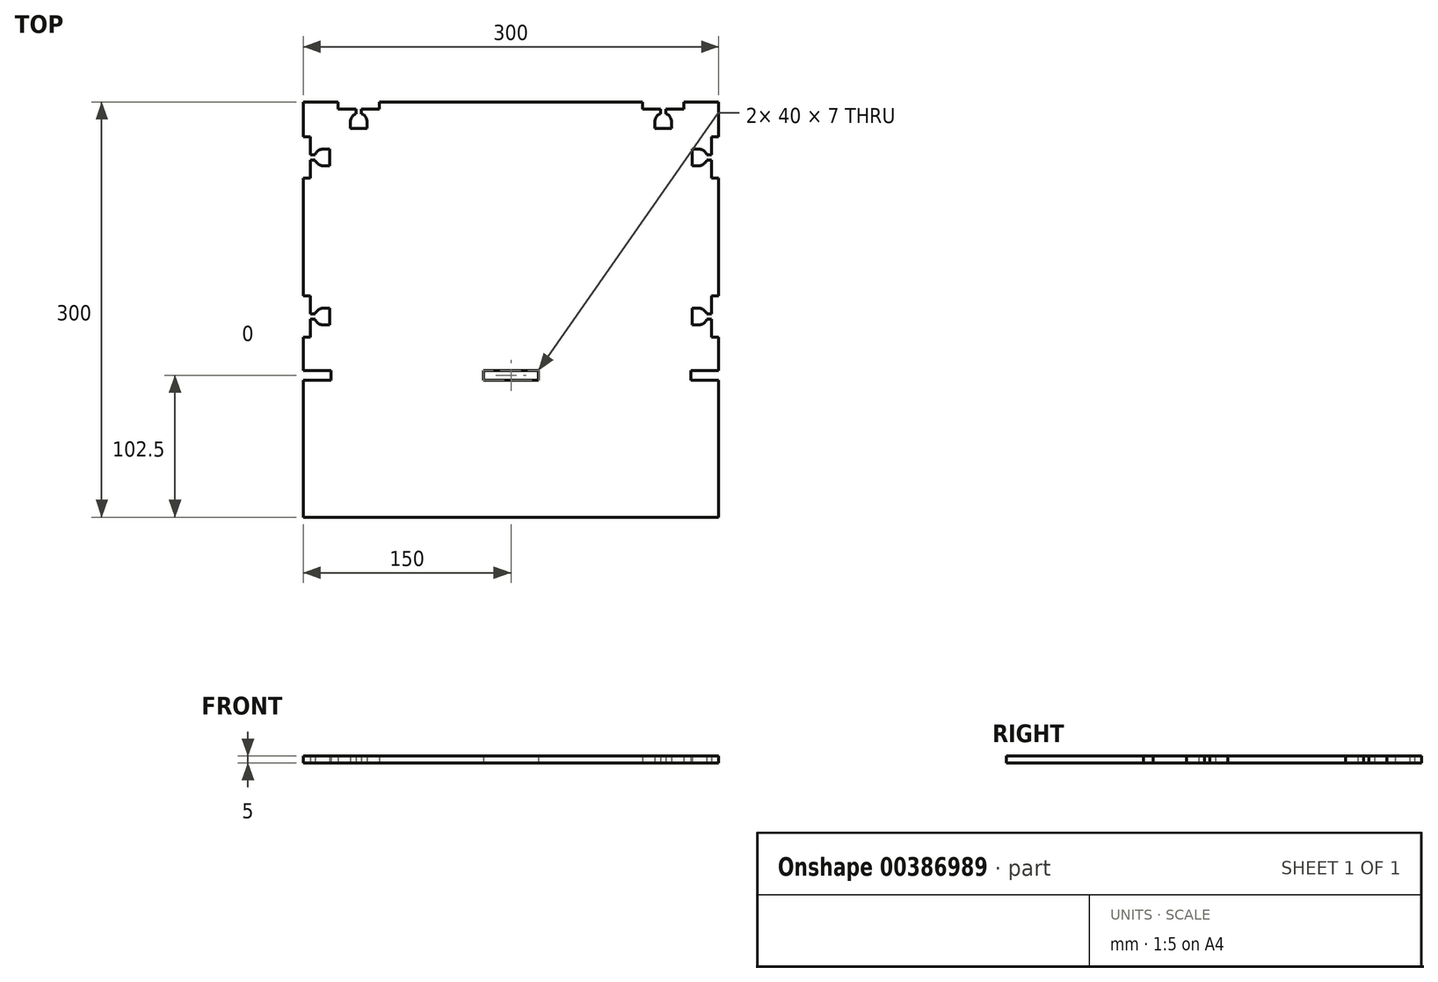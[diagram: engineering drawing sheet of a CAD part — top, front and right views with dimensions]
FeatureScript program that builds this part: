
annotation { "Feature Type Name" : "Feature", "Feature Type Description" : "" }
export const myFeature = defineFeature(function(context is Context, id is Id, definition is map)
    precondition{}
    {
        {
            var Q0;
            Q0=qCreatedBy(makeId("Top.planeOp"),FACE);
            var sketch = newSketch(context, id + "F0", { "sketchPlane" : qUnion([Q0])});
            skLineSegment(sketch, "E0.bottom", {"start": v(0, 0) * mm, "end": v(25, 0) * mm});
            skLineSegment(sketch, "E0.top", {"start": v(0, -300) * mm, "end": v(300, -300) * mm});
            skLineSegment(sketch, "E0.left", {"start": v(0, 0) * mm, "end": v(0, -25) * mm});
            skLineSegment(sketch, "E0.right", {"start": v(300, 0) * mm, "end": v(300, -25) * mm});
            skLineSegment(sketch, "E1.bottom", {"start": v(0, -201) * mm, "end": v(20, -201) * mm});
            skLineSegment(sketch, "E1.top", {"start": v(0, -194) * mm, "end": v(20, -194) * mm});
            skLineSegment(sketch, "E1.right", {"start": v(20, -201) * mm, "end": v(20, -194) * mm});
            skLineSegment(sketch, "E2.bottom", {"start": v(130, -194) * mm, "end": v(170, -194) * mm});
            skLineSegment(sketch, "E2.top", {"start": v(130, -201) * mm, "end": v(170, -201) * mm});
            skLineSegment(sketch, "E2.left", {"start": v(130, -194) * mm, "end": v(130, -201) * mm});
            skLineSegment(sketch, "E2.right", {"start": v(170, -194) * mm, "end": v(170, -201) * mm});
            skLineSegment(sketch, "E3.bottom", {"start": v(280, -194) * mm, "end": v(300, -194) * mm});
            skLineSegment(sketch, "E3.top", {"start": v(280, -201) * mm, "end": v(300, -201) * mm});
            skLineSegment(sketch, "E3.left", {"start": v(280, -194) * mm, "end": v(280, -201) * mm});
            skLineSegment(sketch, "E4.trimOffspring", {"start": v(0, -201) * mm, "end": v(0, -300) * mm});
            skLineSegment(sketch, "E5.trimOffspring", {"start": v(300, -201) * mm, "end": v(300, -300) * mm});
            skLineSegment(sketch, "E6", {"start": v(19.16, -34) * mm, "end": v(19.16, -46) * mm});
            skLineSegment(sketch, "E7", {"start": v(19.16, -34) * mm, "end": v(14.16, -34) * mm});
            skLineSegment(sketch, "E8", {"start": v(19.16, -46) * mm, "end": v(14.16, -46) * mm});
            skLineSegment(sketch, "E9", {"start": v(5, -38) * mm, "end": v(8.5, -38) * mm});
            skLineSegment(sketch, "E10", {"start": v(5, -42) * mm, "end": v(8.5, -42) * mm});
            skArc(sketch, "E11", {"start": v(14.16, -34) * mm, "mid": v(10.7, -35.1) * mm, "end": v(8.5, -38) * mm});
            skArc(sketch, "E12.trimOffspring", {"start": v(8.5, -42) * mm, "mid": v(10.7, -44.9) * mm, "end": v(14.16, -46) * mm});
            skLineSegment(sketch, "E13.bottom", {"start": v(0, -25) * mm, "end": v(5, -25) * mm});
            skLineSegment(sketch, "E13.top", {"start": v(0, -55) * mm, "end": v(5, -55) * mm});
            skLineSegment(sketch, "E13.right", {"start": v(5, -25) * mm, "end": v(5, -38) * mm});
            skLineSegment(sketch, "E14.trimOffspring", {"start": v(5, -42) * mm, "end": v(5, -55) * mm});
            skLineSegment(sketch, "E15", {"start": v(19.16, -149) * mm, "end": v(19.16, -161) * mm});
            skLineSegment(sketch, "E16", {"start": v(19.16, -149) * mm, "end": v(14.16, -149) * mm});
            skLineSegment(sketch, "E17", {"start": v(19.16, -161) * mm, "end": v(14.16, -161) * mm});
            skLineSegment(sketch, "E18", {"start": v(5, -153) * mm, "end": v(8.5, -153) * mm});
            skLineSegment(sketch, "E19", {"start": v(5, -157) * mm, "end": v(8.5, -157) * mm});
            skArc(sketch, "E20", {"start": v(14.16, -149) * mm, "mid": v(10.7, -150.1) * mm, "end": v(8.5, -153) * mm});
            skArc(sketch, "E21.trimOffspring", {"start": v(8.5, -157) * mm, "mid": v(10.7, -159.9) * mm, "end": v(14.16, -161) * mm});
            skLineSegment(sketch, "E22.bottom", {"start": v(0, -140) * mm, "end": v(5, -140) * mm});
            skLineSegment(sketch, "E22.top", {"start": v(0, -170) * mm, "end": v(5, -170) * mm});
            skLineSegment(sketch, "E22.right", {"start": v(5, -140) * mm, "end": v(5, -153) * mm});
            skLineSegment(sketch, "E23.trimOffspring", {"start": v(5, -157) * mm, "end": v(5, -170) * mm});
            skLineSegment(sketch, "E24", {"start": v(46, -19.16) * mm, "end": v(34, -19.16) * mm});
            skLineSegment(sketch, "E25", {"start": v(46, -19.16) * mm, "end": v(46, -14.16) * mm});
            skLineSegment(sketch, "E26", {"start": v(34, -19.16) * mm, "end": v(34, -14.16) * mm});
            skLineSegment(sketch, "E27", {"start": v(42, -5) * mm, "end": v(42, -8.5) * mm});
            skLineSegment(sketch, "E28", {"start": v(38, -5) * mm, "end": v(38, -8.5) * mm});
            skArc(sketch, "E29", {"start": v(46, -14.16) * mm, "mid": v(44.9, -10.7) * mm, "end": v(42, -8.5) * mm});
            skArc(sketch, "E30.trimOffspring", {"start": v(38, -8.5) * mm, "mid": v(35.1, -10.7) * mm, "end": v(34, -14.16) * mm});
            skLineSegment(sketch, "E31.bottom", {"start": v(55, 0) * mm, "end": v(55, -5) * mm});
            skLineSegment(sketch, "E31.top", {"start": v(25, 0) * mm, "end": v(25, -5) * mm});
            skLineSegment(sketch, "E31.right", {"start": v(55, -5) * mm, "end": v(42, -5) * mm});
            skLineSegment(sketch, "E32.trimOffspring", {"start": v(38, -5) * mm, "end": v(25, -5) * mm});
            skLineSegment(sketch, "E33", {"start": v(266, -19.16) * mm, "end": v(254, -19.16) * mm});
            skLineSegment(sketch, "E34", {"start": v(266, -19.16) * mm, "end": v(266, -14.16) * mm});
            skLineSegment(sketch, "E35", {"start": v(254, -19.16) * mm, "end": v(254, -14.16) * mm});
            skLineSegment(sketch, "E36", {"start": v(262, -5) * mm, "end": v(262, -8.5) * mm});
            skLineSegment(sketch, "E37", {"start": v(258, -5) * mm, "end": v(258, -8.5) * mm});
            skArc(sketch, "E38", {"start": v(266, -14.16) * mm, "mid": v(264.9, -10.7) * mm, "end": v(262, -8.5) * mm});
            skArc(sketch, "E39.trimOffspring", {"start": v(258, -8.5) * mm, "mid": v(255.1, -10.7) * mm, "end": v(254, -14.16) * mm});
            skLineSegment(sketch, "E40.bottom", {"start": v(275, 0) * mm, "end": v(275, -5) * mm});
            skLineSegment(sketch, "E40.top", {"start": v(245, 0) * mm, "end": v(245, -5) * mm});
            skLineSegment(sketch, "E40.right", {"start": v(275, -5) * mm, "end": v(262, -5) * mm});
            skLineSegment(sketch, "E41.trimOffspring", {"start": v(258, -5) * mm, "end": v(245, -5) * mm});
            skLineSegment(sketch, "E42", {"start": v(280.84, -46) * mm, "end": v(280.84, -34) * mm});
            skLineSegment(sketch, "E43", {"start": v(280.84, -46) * mm, "end": v(285.84, -46) * mm});
            skLineSegment(sketch, "E44", {"start": v(280.84, -34) * mm, "end": v(285.84, -34) * mm});
            skLineSegment(sketch, "E45", {"start": v(295, -42) * mm, "end": v(291.5, -42) * mm});
            skLineSegment(sketch, "E46", {"start": v(295, -38) * mm, "end": v(291.5, -38) * mm});
            skArc(sketch, "E47", {"start": v(285.84, -46) * mm, "mid": v(289.3, -44.9) * mm, "end": v(291.5, -42) * mm});
            skArc(sketch, "E48.trimOffspring", {"start": v(291.5, -38) * mm, "mid": v(289.3, -35.1) * mm, "end": v(285.84, -34) * mm});
            skLineSegment(sketch, "E49.bottom", {"start": v(300, -55) * mm, "end": v(295, -55) * mm});
            skLineSegment(sketch, "E49.top", {"start": v(300, -25) * mm, "end": v(295, -25) * mm});
            skLineSegment(sketch, "E49.right", {"start": v(295, -55) * mm, "end": v(295, -42) * mm});
            skLineSegment(sketch, "E50.trimOffspring", {"start": v(295, -38) * mm, "end": v(295, -25) * mm});
            skLineSegment(sketch, "E51", {"start": v(280.84, -161) * mm, "end": v(280.84, -149) * mm});
            skLineSegment(sketch, "E52", {"start": v(280.84, -161) * mm, "end": v(285.84, -161) * mm});
            skLineSegment(sketch, "E53", {"start": v(280.84, -149) * mm, "end": v(285.84, -149) * mm});
            skLineSegment(sketch, "E54", {"start": v(295, -157) * mm, "end": v(291.5, -157) * mm});
            skLineSegment(sketch, "E55", {"start": v(295, -153) * mm, "end": v(291.5, -153) * mm});
            skArc(sketch, "E56", {"start": v(285.84, -161) * mm, "mid": v(289.3, -159.9) * mm, "end": v(291.5, -157) * mm});
            skArc(sketch, "E57.trimOffspring", {"start": v(291.5, -153) * mm, "mid": v(289.3, -150.1) * mm, "end": v(285.84, -149) * mm});
            skLineSegment(sketch, "E58.bottom", {"start": v(300, -170) * mm, "end": v(295, -170) * mm});
            skLineSegment(sketch, "E58.top", {"start": v(300, -140) * mm, "end": v(295, -140) * mm});
            skLineSegment(sketch, "E58.right", {"start": v(295, -170) * mm, "end": v(295, -157) * mm});
            skLineSegment(sketch, "E59.trimOffspring", {"start": v(295, -153) * mm, "end": v(295, -140) * mm});
            skLineSegment(sketch, "E60.trimOffspring", {"start": v(300, -170) * mm, "end": v(300, -194) * mm});
            skLineSegment(sketch, "E61.trimOffspring", {"start": v(0, -170) * mm, "end": v(0, -194) * mm});
            skLineSegment(sketch, "E62.trimOffspring", {"start": v(55, 0) * mm, "end": v(245, 0) * mm});
            skLineSegment(sketch, "E63.trimOffspring", {"start": v(0, -55) * mm, "end": v(0, -140) * mm});
            skLineSegment(sketch, "E64.trimOffspring", {"start": v(300, -55) * mm, "end": v(300, -140) * mm});
            skLineSegment(sketch, "E65.trimOffspring", {"start": v(275, 0) * mm, "end": v(300, 0) * mm});
            skSolve(sketch);
        }
        {
            var Q0;
            Q0=makeQuery(id+"F0.imprint","IMPRINT",FACE,{"disambiguationData":[TD([[makeQuery(id+"F0.imprint","IMPRINT",EDGE,{"derivedFrom":sQuery(id+"F0.wireOp",EDGE,"E0.bottom")}),-1.0]])]});
            extrude(context, id + "F1", {"entities" : qUnion([Q0]), "depth" : 5 * mm});
        }
    });
